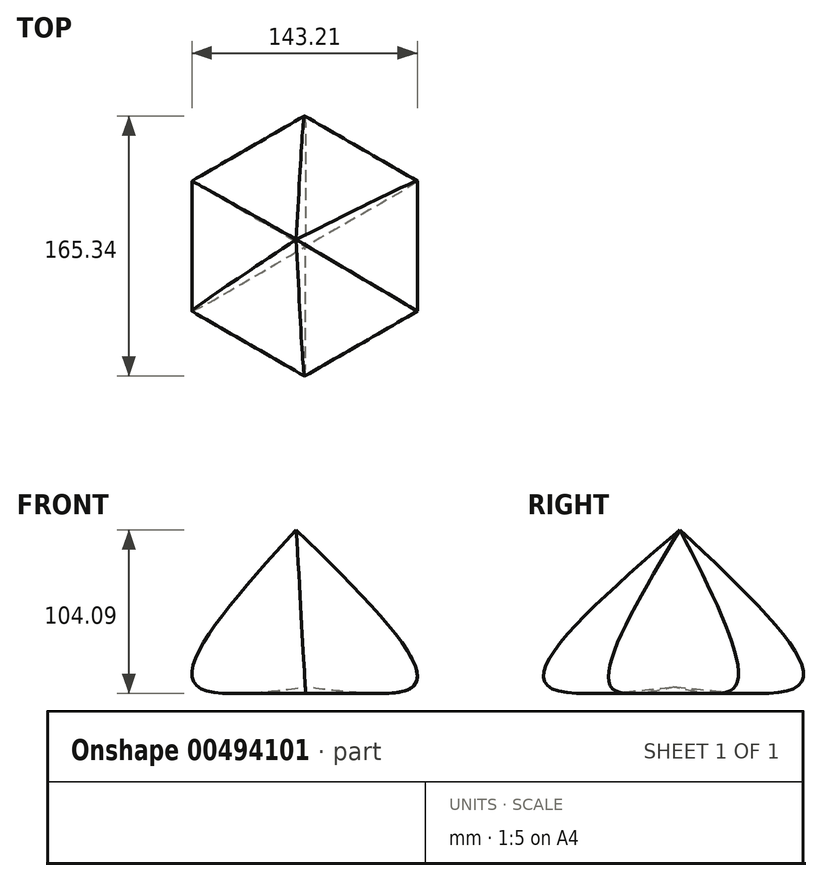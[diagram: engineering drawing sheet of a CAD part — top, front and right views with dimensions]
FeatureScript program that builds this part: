
annotation { "Feature Type Name" : "Feature", "Feature Type Description" : "" }
export const myFeature = defineFeature(function(context is Context, id is Id, definition is map)
    precondition{}
    {
        {
            var Q0;
            Q0=qCreatedBy(makeId("Top.planeOp"),FACE);
            var sketch = newSketch(context, id + "F0", { "sketchPlane" : qUnion([Q0])});
            skCircle(sketch, "E0.cCircle", {"center": v(0, 0) * mm, "radius": 78.46 * mm, "construction": true});
            skLineSegment(sketch, "E0.0", {"start": v(0, 78.46) * mm, "end": v(67.95, 39.23) * mm});
            skLineSegment(sketch, "E0.1", {"start": v(67.95, 39.23) * mm, "end": v(67.95, -39.23) * mm});
            skLineSegment(sketch, "E0.2", {"start": v(67.95, -39.23) * mm, "end": v(0, -78.46) * mm});
            skLineSegment(sketch, "E0.3", {"start": v(0, -78.46) * mm, "end": v(-67.95, -39.23) * mm});
            skLineSegment(sketch, "E0.4", {"start": v(-67.95, -39.23) * mm, "end": v(-67.95, 39.23) * mm});
            skLineSegment(sketch, "E0.5", {"start": v(-67.95, 39.23) * mm, "end": v(0, 78.46) * mm});
            skSolve(sketch);
        }
        {
            var Q0;
            Q0=qCreatedBy(makeId("Top.planeOp"),FACE);
            cPlane(context, id + "F1", {"entities" : qUnion([Q0]), "cplaneType" : CPlaneType.OFFSET, "offset" : 100 * mm, "width" : 150 * mm, "height" : 150 * mm});
        }
        {
            var Q0;
            Q0=qCreatedBy(id+"F1.planeOp",FACE);
            var sketch = newSketch(context, id + "F2", { "sketchPlane" : qUnion([Q0])});
            skPoint(sketch, "E1", {"position": v(-5.74, 4.45) * mm});
            skSolve(sketch);
        }
        {
            var Q0;
            Q0=sQuery(id+"F2.wireOp",VERTEX,"E1");
            var Q1;
            Q1=makeQuery(id+"F0.imprint","IMPRINT",FACE,{"disambiguationData":[TD([[makeQuery(id+"F0.imprint","IMPRINT",EDGE,{"derivedFrom":sQuery(id+"F0.wireOp",EDGE,"E0.0")}),-1.0]])]});
            var Q2;
            Q2=sQuery(id+"F0.wireOp",VERTEX,"E0.cCircle.center");
            loft(context, id + "F3", {"sheetProfilesArray" : [{ "sheetProfileEntities" : qUnion([Q0]) }, { "sheetProfileEntities" : qUnion([Q1]) }, { "sheetProfileEntities" : qUnion([Q2]) }]});
        }
    });
